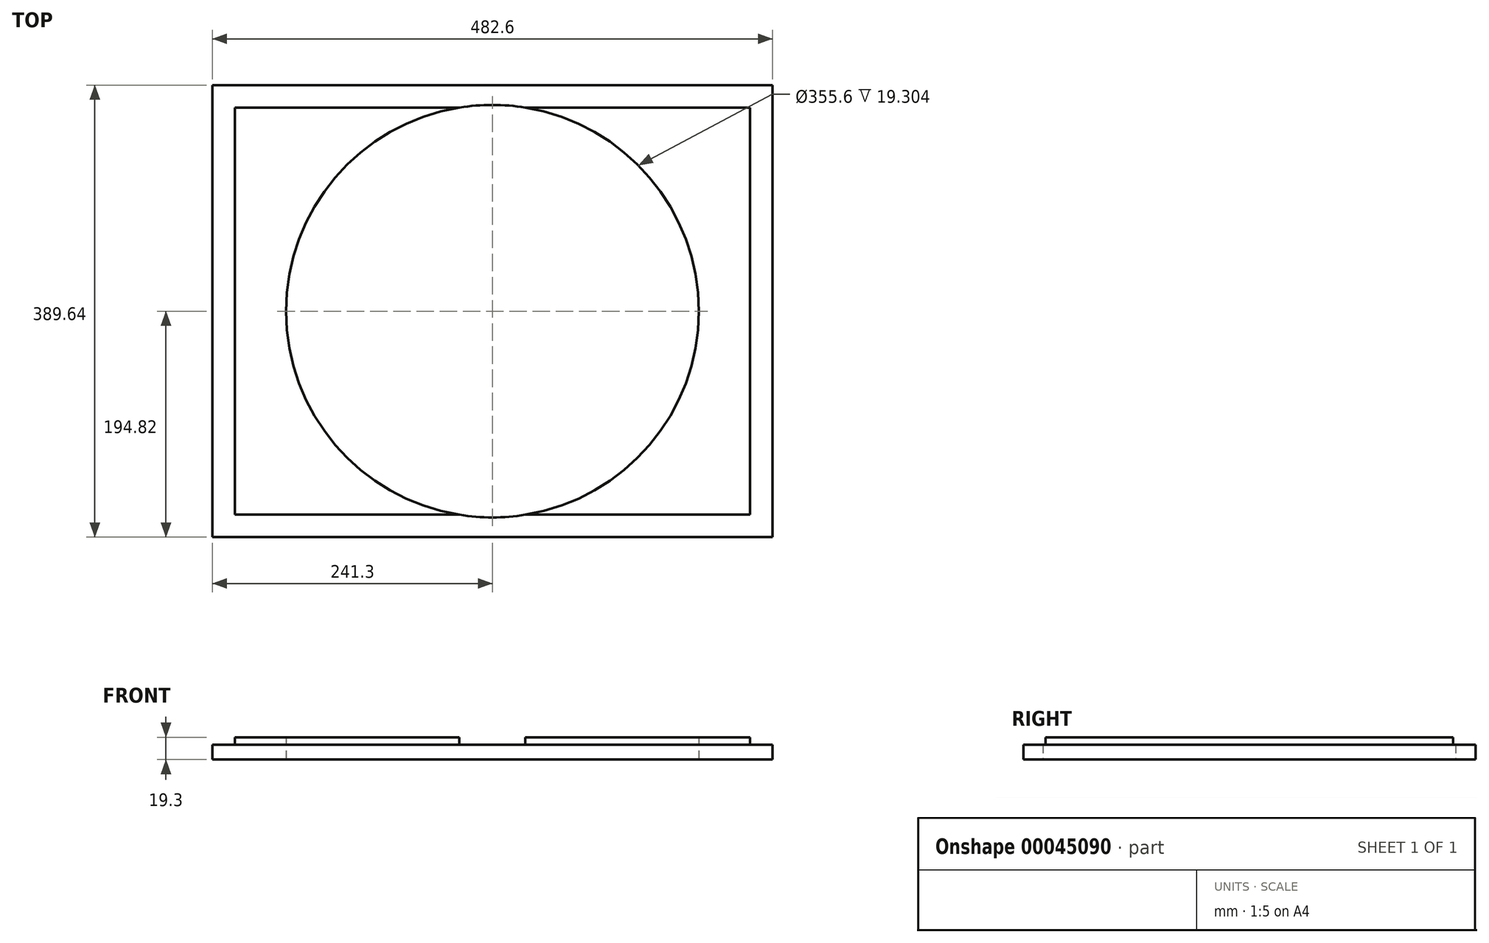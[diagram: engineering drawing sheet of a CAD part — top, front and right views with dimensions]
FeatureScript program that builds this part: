
annotation { "Feature Type Name" : "Feature", "Feature Type Description" : "" }
export const myFeature = defineFeature(function(context is Context, id is Id, definition is map)
    precondition{}
    {
        {
            var Q0;
            Q0=qCreatedBy(makeId("Top.planeOp"),FACE);
            var sketch = newSketch(context, id + "F0", { "sketchPlane" : qUnion([Q0])});
            skLineSegment(sketch, "E0.rect.bottom", {"start": v(-241.3, 194.82) * mm, "end": v(241.3, 194.82) * mm});
            skLineSegment(sketch, "E0.rect.top", {"start": v(-241.3, -194.82) * mm, "end": v(241.3, -194.82) * mm});
            skLineSegment(sketch, "E0.rect.left", {"start": v(-241.3, 194.82) * mm, "end": v(-241.3, -194.82) * mm});
            skLineSegment(sketch, "E0.rect.right", {"start": v(241.3, 194.82) * mm, "end": v(241.3, -194.82) * mm});
            skPoint(sketch, "E0.rect.middle", {"position": v(0, 0) * mm});
            skSolve(sketch);
        }
        {
            var Q0;
            Q0 = qSketchRegion(id + "F0", true);
            extrude(context, id + "F1", {"entities" : qUnion([Q0]), "depth" : 19.3 * mm});
        }
        {
            var Q0;
            Q0=sQuery(id+"F0.wireOp",VERTEX,"E0.rect.middle");
            var Q1;
            Q1=makeQuery(id+"F1.opExtrude","SWEPT_BODY",BODY,{"disambiguationData":[OSD([sQuery(id+"F0.wireOp",EDGE,"E0.rect.bottom"),sQuery(id+"F0.wireOp",EDGE,"E0.rect.top"),sQuery(id+"F0.wireOp",EDGE,"E0.rect.left"),sQuery(id+"F0.wireOp",EDGE,"E0.rect.right")])]});
            hole(context, id + "F2", {"style" : HoleStyle.SIMPLE, "holeDiameter" : 355.6 * mm, "endStyle" : HoleEndStyle.THROUGH, "oppositeDirection" : true, "locations" : qUnion([Q0]), "scope" : qUnion([Q1])});
        }
        {
            var Q0;
            Q0=makeQuery(id+"F1.opExtrude","CAP_FACE",FACE,{"disambiguationData":[OSD([sQuery(id+"F0.wireOp",EDGE,"E0.rect.bottom"),sQuery(id+"F0.wireOp",EDGE,"E0.rect.top"),sQuery(id+"F0.wireOp",EDGE,"E0.rect.left"),sQuery(id+"F0.wireOp",EDGE,"E0.rect.right")])],"isStart":false});
            var sketch = newSketch(context, id + "F3", { "sketchPlane" : qUnion([Q0])});
            skLineSegment(sketch, "E1.bottom", {"start": v(-241.3, 194.82) * mm, "end": v(241.3, 194.82) * mm});
            skLineSegment(sketch, "E1.top", {"start": v(-241.3, 175.51) * mm, "end": v(241.3, 175.51) * mm});
            skLineSegment(sketch, "E1.left", {"start": v(-241.3, 194.82) * mm, "end": v(-241.3, 175.51) * mm});
            skLineSegment(sketch, "E1.right", {"start": v(241.3, 194.82) * mm, "end": v(241.3, 175.51) * mm});
            skLineSegment(sketch, "E2.bottom", {"start": v(-241.3, -194.82) * mm, "end": v(241.3, -194.82) * mm});
            skLineSegment(sketch, "E2.top", {"start": v(-241.3, -175.51) * mm, "end": v(241.3, -175.51) * mm});
            skLineSegment(sketch, "E2.left", {"start": v(-241.3, -194.82) * mm, "end": v(-241.3, -175.51) * mm});
            skLineSegment(sketch, "E2.right", {"start": v(241.3, -194.82) * mm, "end": v(241.3, -175.51) * mm});
            skLineSegment(sketch, "E3.bottom", {"start": v(-241.3, 194.82) * mm, "end": v(-222, 194.82) * mm});
            skLineSegment(sketch, "E3.top", {"start": v(-241.3, -194.82) * mm, "end": v(-222, -194.82) * mm});
            skLineSegment(sketch, "E3.left", {"start": v(-241.3, 194.82) * mm, "end": v(-241.3, -194.82) * mm});
            skLineSegment(sketch, "E3.right", {"start": v(-222, 194.82) * mm, "end": v(-222, -194.82) * mm});
            skLineSegment(sketch, "E4.bottom", {"start": v(241.3, 194.82) * mm, "end": v(222, 194.82) * mm});
            skLineSegment(sketch, "E4.top", {"start": v(241.3, -194.82) * mm, "end": v(222, -194.82) * mm});
            skLineSegment(sketch, "E4.left", {"start": v(241.3, 194.82) * mm, "end": v(241.3, -194.82) * mm});
            skLineSegment(sketch, "E4.right", {"start": v(222, 194.82) * mm, "end": v(222, -194.82) * mm});
            skSolve(sketch);
        }
        {
            var Q0;
            Q0 = qSketchRegion(id + "F3", true);
            extrude(context, id + "F4", {"entities" : qUnion([Q0]), "operationType" : NewBodyOperationType.REMOVE, "oppositeDirection" : true, "depth" : 6.35 * mm});
        }
    });
